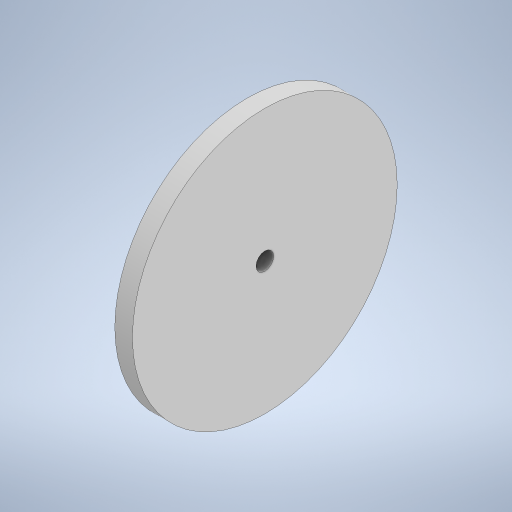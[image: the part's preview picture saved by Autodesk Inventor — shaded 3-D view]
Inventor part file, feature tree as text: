
AUTODESK INVENTOR PART (.ipt)
format: ipt  version: 2023.2 (Build 272271000, 271)  size: 247,296 bytes
history: native  units: mm
features: sketch x1, extrude x1, hole x1
ambient origin geometry x8: Origin, YZ Plane, XZ Plane, XY Plane, X Axis, Y Axis, Z Axis, Center Point
bodies: Body1 (feature_tree)
feature tree (3):
  sketch  "Sketch14"  dims[d228=60.0mm d229=4.0mm d230=0.0mm d231=4.0mm d232=6.0mm d233=4.0mm d234=2.0mm d235=90.0deg d236=8.0mm d237=20.594885mm d9=0.5mm d10=0.872665mm d11=0.5mm d12=0.872665mm d13=0.5mm d14=0.872665mm d27=0.5mm d28=0.872665mm d29=0.5mm d30=0.872665mm d88=0.5mm d89=0.872665mm d90=0.5mm d91=0.872665mm d116=0.5mm d117=0.872665mm d118=0.5mm d119=0.872665mm d154=0.5mm d155=0.872665mm d156=0.5mm d157=0.872665mm d181=0.5mm d182=0.872665mm d183=0.5mm d184=0.872665mm d221=0.5mm d222=0.872665mm d223=0.5mm d224=0.872665mm]
  extrude  "Extrusion16"  Depth=4.0mm TaperAngle=0.0deg
  hole  "Hole3"  [1 undecoded]
note: 1 required parameter value undecoded (feature->parameter linkage not recoverable at this tier; creation-order binding heuristic only, values carry confidence <= 0.55)
